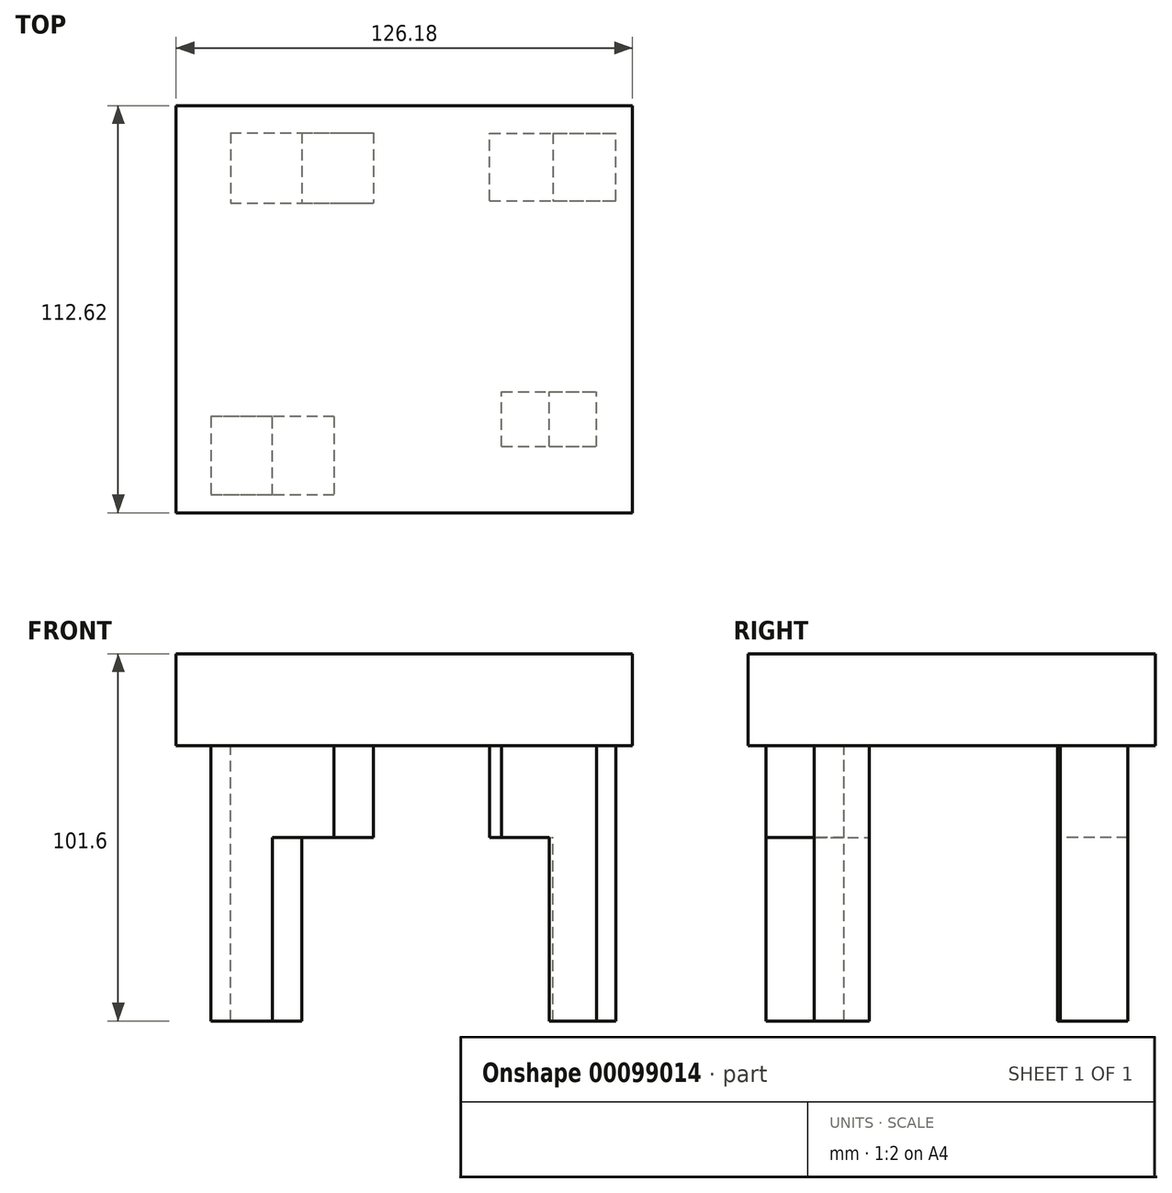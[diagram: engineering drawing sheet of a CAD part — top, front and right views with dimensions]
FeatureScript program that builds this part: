
annotation { "Feature Type Name" : "Feature", "Feature Type Description" : "" }
export const myFeature = defineFeature(function(context is Context, id is Id, definition is map)
    precondition{}
    {
        {
            var Q0;
            Q0=qCreatedBy(makeId("Top.planeOp"),FACE);
            var sketch = newSketch(context, id + "F0", { "sketchPlane" : qUnion([Q0])});
            skLineSegment(sketch, "E0.bottom", {"start": v(-67.69, 61.67) * mm, "end": v(58.49, 61.67) * mm});
            skLineSegment(sketch, "E0.top", {"start": v(-67.69, -50.95) * mm, "end": v(58.49, -50.95) * mm});
            skLineSegment(sketch, "E0.left", {"start": v(-67.69, 61.67) * mm, "end": v(-67.69, -50.95) * mm});
            skLineSegment(sketch, "E0.right", {"start": v(58.49, 61.67) * mm, "end": v(58.49, -50.95) * mm});
            skSolve(sketch);
        }
        {
            var Q0;
            Q0=makeQuery(id+"F0.imprint","IMPRINT",FACE,{"disambiguationData":[TD([[makeQuery(id+"F0.imprint","IMPRINT",EDGE,{"derivedFrom":sQuery(id+"F0.wireOp",EDGE,"E0.bottom")}),-1.0]])]});
            extrude(context, id + "F1", {"entities" : qUnion([Q0]), "depth" : 25.4 * mm});
        }
        {
            var Q0;
            Q0=makeQuery(id+"F1.opExtrude","CAP_FACE",FACE,{"disambiguationData":[OSD([sQuery(id+"F0.wireOp",EDGE,"E0.bottom"),sQuery(id+"F0.wireOp",EDGE,"E0.top"),sQuery(id+"F0.wireOp",EDGE,"E0.left"),sQuery(id+"F0.wireOp",EDGE,"E0.right")])],"isStart":true});
            var sketch = newSketch(context, id + "F2", { "sketchPlane" : qUnion([Q0])});
            skLineSegment(sketch, "E1.bottom", {"start": v(22.34, 32.62) * mm, "end": v(48.66, 32.62) * mm});
            skLineSegment(sketch, "E1.top", {"start": v(22.34, 17.42) * mm, "end": v(48.66, 17.42) * mm});
            skLineSegment(sketch, "E1.left", {"start": v(22.34, 32.62) * mm, "end": v(22.34, 17.42) * mm});
            skLineSegment(sketch, "E1.right", {"start": v(48.66, 32.62) * mm, "end": v(48.66, 17.42) * mm});
            skSolve(sketch);
        }
        {
            var Q0;
            Q0=makeQuery(id+"F2.imprint","IMPRINT",FACE,{"disambiguationData":[TD([[makeQuery(id+"F2.imprint","IMPRINT",EDGE,{"derivedFrom":sQuery(id+"F2.wireOp",EDGE,"E1.bottom")}),-1.0]])]});
            extrude(context, id + "F3", {"entities" : qUnion([Q0]), "operationType" : NewBodyOperationType.ADD, "depth" : 25.4 * mm});
        }
        {
            var Q0;
            Q0=makeQuery(id+"F1.opExtrude","CAP_FACE",FACE,{"disambiguationData":[OSD([sQuery(id+"F0.wireOp",EDGE,"E0.bottom"),sQuery(id+"F0.wireOp",EDGE,"E0.top"),sQuery(id+"F0.wireOp",EDGE,"E0.left"),sQuery(id+"F0.wireOp",EDGE,"E0.right")])],"isStart":true});
            var sketch = newSketch(context, id + "F4", { "sketchPlane" : qUnion([Q0])});
            skLineSegment(sketch, "E2.bottom", {"start": v(-24, 24.4) * mm, "end": v(-58.13, 24.4) * mm});
            skLineSegment(sketch, "E2.top", {"start": v(-24, 46) * mm, "end": v(-58.13, 46) * mm});
            skLineSegment(sketch, "E2.left", {"start": v(-24, 24.4) * mm, "end": v(-24, 46) * mm});
            skLineSegment(sketch, "E2.right", {"start": v(-58.13, 24.4) * mm, "end": v(-58.13, 46) * mm});
            skSolve(sketch);
        }
        {
            var Q0;
            Q0 = qSketchRegion(id + "F4", true);
            extrude(context, id + "F5", {"entities" : qUnion([Q0]), "operationType" : NewBodyOperationType.ADD, "depth" : 25.4 * mm});
        }
        {
            var Q0;
            Q0=makeQuery(id+"F1.opExtrude","CAP_FACE",FACE,{"disambiguationData":[OSD([sQuery(id+"F0.wireOp",EDGE,"E0.bottom"),sQuery(id+"F0.wireOp",EDGE,"E0.top"),sQuery(id+"F0.wireOp",EDGE,"E0.left"),sQuery(id+"F0.wireOp",EDGE,"E0.right")])],"isStart":true});
            var sketch = newSketch(context, id + "F6", { "sketchPlane" : qUnion([Q0])});
            skLineSegment(sketch, "E3.bottom", {"start": v(-52.66, -54.15) * mm, "end": v(-13.07, -54.15) * mm});
            skLineSegment(sketch, "E3.top", {"start": v(-52.66, -34.66) * mm, "end": v(-13.07, -34.66) * mm});
            skLineSegment(sketch, "E3.left", {"start": v(-52.66, -54.15) * mm, "end": v(-52.66, -34.66) * mm});
            skLineSegment(sketch, "E3.right", {"start": v(-13.07, -54.15) * mm, "end": v(-13.07, -34.66) * mm});
            skSolve(sketch);
        }
        {
            var Q0;
            Q0=makeQuery(id+"F1.opExtrude","CAP_FACE",FACE,{"disambiguationData":[OSD([sQuery(id+"F0.wireOp",EDGE,"E0.bottom"),sQuery(id+"F0.wireOp",EDGE,"E0.top"),sQuery(id+"F0.wireOp",EDGE,"E0.left"),sQuery(id+"F0.wireOp",EDGE,"E0.right")])],"isStart":true});
            var sketch = newSketch(context, id + "F7", { "sketchPlane" : qUnion([Q0])});
            skLineSegment(sketch, "E4.bottom", {"start": v(19.07, -35.38) * mm, "end": v(53.93, -35.38) * mm});
            skLineSegment(sketch, "E4.top", {"start": v(19.07, -54.07) * mm, "end": v(53.93, -54.07) * mm});
            skLineSegment(sketch, "E4.left", {"start": v(19.07, -35.38) * mm, "end": v(19.07, -54.07) * mm});
            skLineSegment(sketch, "E4.right", {"start": v(53.93, -35.38) * mm, "end": v(53.93, -54.07) * mm});
            skSolve(sketch);
        }
        {
            var Q0;
            Q0 = qSketchRegion(id + "F7", true);
            extrude(context, id + "F8", {"entities" : qUnion([Q0]), "operationType" : NewBodyOperationType.ADD, "depth" : 25.4 * mm});
        }
        {
            var Q0;
            Q0=makeQuery(id+"F5.opExtrude","CAP_FACE",FACE,{"disambiguationData":[OSD([sQuery(id+"F4.wireOp",EDGE,"E2.bottom"),sQuery(id+"F4.wireOp",EDGE,"E2.top"),sQuery(id+"F4.wireOp",EDGE,"E2.left"),sQuery(id+"F4.wireOp",EDGE,"E2.right")])],"isStart":false});
            var sketch = newSketch(context, id + "F9", { "sketchPlane" : qUnion([Q0])});
            skLineSegment(sketch, "E5.bottom", {"start": v(-58.13, 46) * mm, "end": v(-41.06, 46) * mm});
            skLineSegment(sketch, "E5.top", {"start": v(-58.13, 24.4) * mm, "end": v(-41.06, 24.4) * mm});
            skLineSegment(sketch, "E5.left", {"start": v(-58.13, 46) * mm, "end": v(-58.13, 24.4) * mm});
            skLineSegment(sketch, "E5.right", {"start": v(-41.06, 46) * mm, "end": v(-41.06, 24.4) * mm});
            skSolve(sketch);
        }
        {
            var Q0;
            Q0=makeQuery(id+"F3.opExtrude","CAP_FACE",FACE,{"disambiguationData":[OSD([sQuery(id+"F2.wireOp",EDGE,"E1.bottom"),sQuery(id+"F2.wireOp",EDGE,"E1.top"),sQuery(id+"F2.wireOp",EDGE,"E1.left"),sQuery(id+"F2.wireOp",EDGE,"E1.right")])],"isStart":false});
            var sketch = newSketch(context, id + "F10", { "sketchPlane" : qUnion([Q0])});
            skLineSegment(sketch, "E6.bottom", {"start": v(35.5, 32.62) * mm, "end": v(48.66, 32.62) * mm});
            skLineSegment(sketch, "E6.top", {"start": v(35.5, 17.42) * mm, "end": v(48.66, 17.42) * mm});
            skLineSegment(sketch, "E6.left", {"start": v(35.5, 32.62) * mm, "end": v(35.5, 17.42) * mm});
            skLineSegment(sketch, "E6.right", {"start": v(48.66, 32.62) * mm, "end": v(48.66, 17.42) * mm});
            skSolve(sketch);
        }
        {
            var Q0;
            Q0=makeQuery(id+"F6.imprint","IMPRINT",FACE,{"disambiguationData":[TD([[makeQuery(id+"F6.imprint","IMPRINT",EDGE,{"derivedFrom":sQuery(id+"F6.wireOp",EDGE,"E3.bottom")}),1.0]])]});
            extrude(context, id + "F11", {"entities" : qUnion([Q0]), "operationType" : NewBodyOperationType.ADD, "depth" : 25.4 * mm});
        }
        {
            var Q0;
            Q0=makeQuery(id+"F9.imprint","IMPRINT",FACE,{"disambiguationData":[TD([[makeQuery(id+"F9.imprint","IMPRINT",EDGE,{"derivedFrom":sQuery(id+"F9.wireOp",EDGE,"E5.bottom")}),1.0]])]});
            extrude(context, id + "F12", {"entities" : qUnion([Q0]), "operationType" : NewBodyOperationType.ADD, "depth" : 50.8 * mm});
        }
        {
            var Q0;
            Q0=makeQuery(id+"F10.imprint","IMPRINT",FACE,{"disambiguationData":[TD([[makeQuery(id+"F10.imprint","IMPRINT",EDGE,{"derivedFrom":sQuery(id+"F10.wireOp",EDGE,"E6.bottom")}),-1.0]])]});
            extrude(context, id + "F13", {"entities" : qUnion([Q0]), "operationType" : NewBodyOperationType.ADD, "depth" : 50.8 * mm});
        }
        {
            var Q0;
            Q0=makeQuery(id+"F8.opExtrude","CAP_FACE",FACE,{"disambiguationData":[OSD([sQuery(id+"F7.wireOp",EDGE,"E4.bottom"),sQuery(id+"F7.wireOp",EDGE,"E4.top"),sQuery(id+"F7.wireOp",EDGE,"E4.left"),sQuery(id+"F7.wireOp",EDGE,"E4.right")])],"isStart":false});
            var sketch = newSketch(context, id + "F14", { "sketchPlane" : qUnion([Q0])});
            skLineSegment(sketch, "E7.bottom", {"start": v(53.93, -54.07) * mm, "end": v(36.5, -54.07) * mm});
            skLineSegment(sketch, "E7.top", {"start": v(53.93, -35.38) * mm, "end": v(36.5, -35.38) * mm});
            skLineSegment(sketch, "E7.left", {"start": v(53.93, -54.07) * mm, "end": v(53.93, -35.38) * mm});
            skLineSegment(sketch, "E7.right", {"start": v(36.5, -54.07) * mm, "end": v(36.5, -35.38) * mm});
            skSolve(sketch);
        }
        {
            var Q0;
            Q0 = qSketchRegion(id + "F14", true);
            extrude(context, id + "F15", {"entities" : qUnion([Q0]), "operationType" : NewBodyOperationType.ADD, "depth" : 50.8 * mm});
        }
        {
            var Q0;
            Q0=makeQuery(id+"F11.opExtrude","CAP_FACE",FACE,{"disambiguationData":[OSD([sQuery(id+"F6.wireOp",EDGE,"E3.bottom"),sQuery(id+"F6.wireOp",EDGE,"E3.top"),sQuery(id+"F6.wireOp",EDGE,"E3.left"),sQuery(id+"F6.wireOp",EDGE,"E3.right")])],"isStart":false});
            var sketch = newSketch(context, id + "F16", { "sketchPlane" : qUnion([Q0])});
            skLineSegment(sketch, "E8.bottom", {"start": v(-32.87, -54.15) * mm, "end": v(-52.66, -54.15) * mm});
            skLineSegment(sketch, "E8.top", {"start": v(-32.87, -34.66) * mm, "end": v(-52.66, -34.66) * mm});
            skLineSegment(sketch, "E8.left", {"start": v(-32.87, -54.15) * mm, "end": v(-32.87, -34.66) * mm});
            skLineSegment(sketch, "E8.right", {"start": v(-52.66, -54.15) * mm, "end": v(-52.66, -34.66) * mm});
            skSolve(sketch);
        }
        {
            var Q0;
            Q0 = qSketchRegion(id + "F16", true);
            extrude(context, id + "F17", {"entities" : qUnion([Q0]), "operationType" : NewBodyOperationType.ADD, "depth" : 50.8 * mm});
        }
    });
